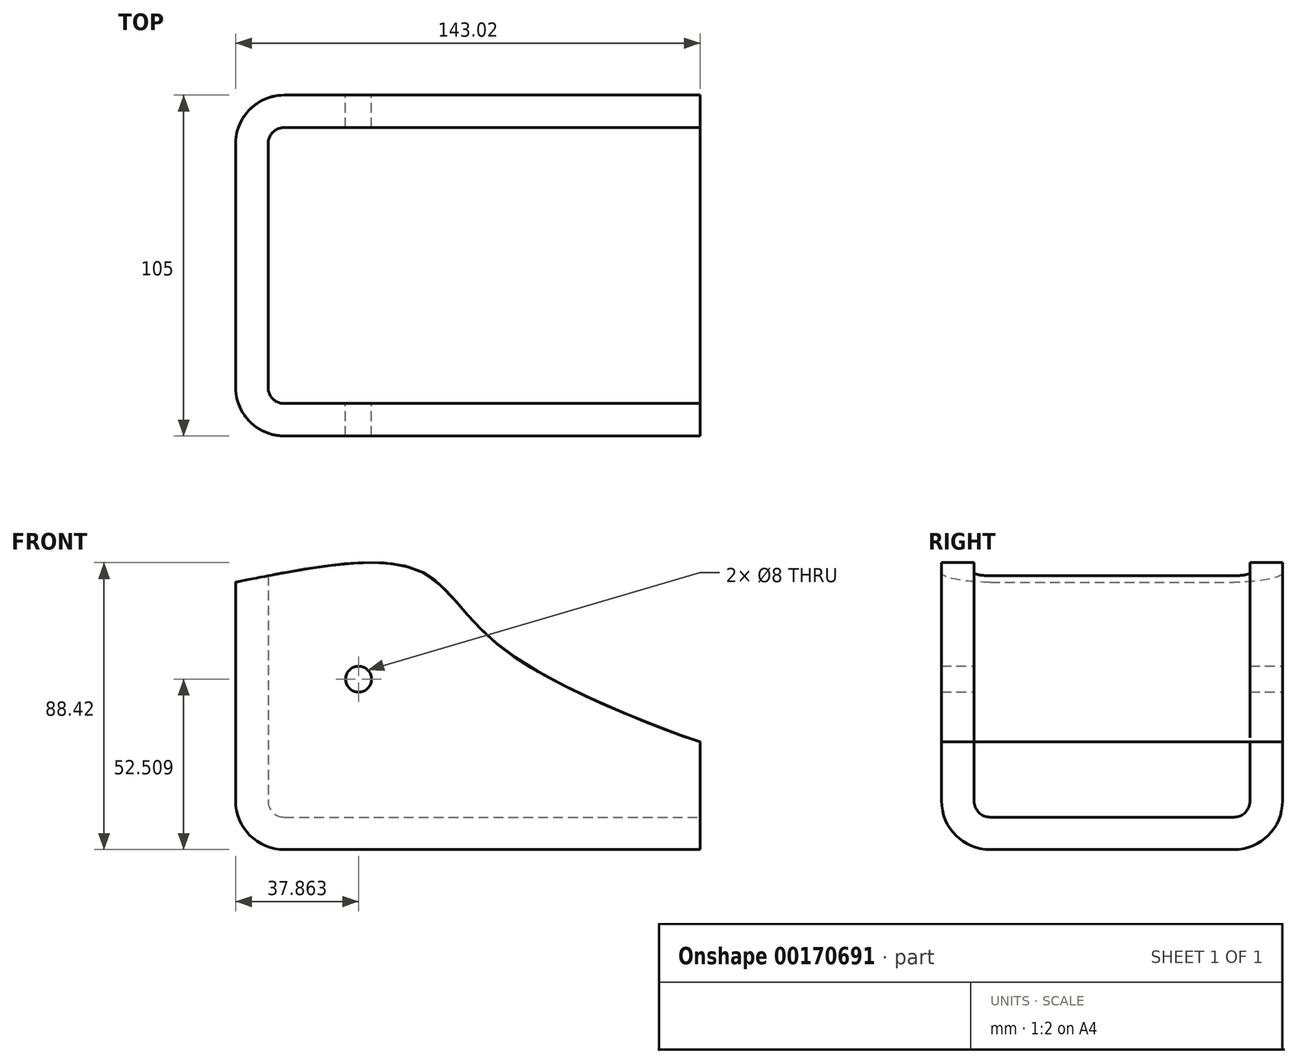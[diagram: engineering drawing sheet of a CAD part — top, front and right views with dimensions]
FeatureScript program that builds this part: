
annotation { "Feature Type Name" : "Feature", "Feature Type Description" : "" }
export const myFeature = defineFeature(function(context is Context, id is Id, definition is map)
    precondition{}
    {
        {
            var Q0;
            Q0=qCreatedBy(makeId("Front.planeOp"),FACE);
            var sketch = newSketch(context, id + "F0", { "sketchPlane" : qUnion([Q0])});
            skLineSegment(sketch, "E0.bottom", {"start": v(-80.05, 54.87) * mm, "end": v(101.14, 54.87) * mm});
            skLineSegment(sketch, "E0.top", {"start": v(-80.05, -66.57) * mm, "end": v(101.14, -66.57) * mm});
            skLineSegment(sketch, "E0.left", {"start": v(-80.05, 54.87) * mm, "end": v(-80.05, -66.57) * mm});
            skLineSegment(sketch, "E0.right", {"start": v(101.14, 54.87) * mm, "end": v(101.14, -66.57) * mm});
            skSolve(sketch);
        }
        {
            var Q0;
            Q0=makeQuery(id+"F0.imprint","IMPRINT",FACE,{"disambiguationData":[TD([[makeQuery(id+"F0.imprint","IMPRINT",EDGE,{"derivedFrom":sQuery(id+"F0.wireOp",EDGE,"E0.bottom")}),-1.0]])]});
            var sketch = newSketch(context, id + "F1", { "sketchPlane" : qUnion([Q0])});
            skSolve(sketch);
        }
        {
            var Q0;
            Q0=makeQuery(id+"F0.imprint","IMPRINT",FACE,{"disambiguationData":[TD([[makeQuery(id+"F0.imprint","IMPRINT",EDGE,{"derivedFrom":sQuery(id+"F0.wireOp",EDGE,"E0.bottom")}),-1.0]])]});
            var Q1;
            Q1=makeQuery(id+"F1.imprint","IMPRINT",FACE,{"disambiguationData":[TD([[makeQuery(id+"F1.imprint","IMPRINT",EDGE,{"derivedFrom":makeQuery(id+"F0.imprint","IMPRINT",EDGE,{"derivedFrom":sQuery(id+"F0.wireOp",EDGE,"E0.bottom")})}),-1.0]])]});
            extrude(context, id + "F2", {"entities" : qUnion([Q0, Q1]), "depth" : 82 * mm});
        }
        {
            var Q0;
            {var subQ0=sQuery(id+"F0.wireOp",EDGE,"E0.right");var subQ1=sQuery(id+"F0.wireOp",EDGE,"E0.left");var subQ2=sQuery(id+"F0.wireOp",EDGE,"E0.top");var subQ3=sQuery(id+"F0.wireOp",EDGE,"E0.bottom");Q0=makeQuery(id+"F2.opExtrude","CAP_FACE",FACE,{"disambiguationData":[OSD([subQ3,subQ2,subQ1,subQ0]),TDD([makeQuery(id+"F0.imprint","IMPRINT",EDGE,{"derivedFrom":subQ3}),makeQuery(id+"F0.imprint","IMPRINT",EDGE,{"derivedFrom":subQ2}),makeQuery(id+"F0.imprint","IMPRINT",EDGE,{"derivedFrom":subQ1}),makeQuery(id+"F0.imprint","IMPRINT",EDGE,{"derivedFrom":subQ0})])],"isStart":false});}
            var sketch = newSketch(context, id + "F3", { "sketchPlane" : qUnion([Q0])});
            skSolve(sketch);
        }
        {
            var Q0;
            {var subQ0=sQuery(id+"F0.wireOp",EDGE,"E0.bottom");Q0=makeQuery(id+"F3.imprint","IMPRINT",FACE,{"disambiguationData":[TD([[makeQuery(id+"F3.imprint","IMPRINT",EDGE,{"derivedFrom":makeQuery(id+"F2.opExtrude","CAP_EDGE",EDGE,{"disambiguationData":[OSD([subQ0]),TDD([makeQuery(id+"F0.imprint","IMPRINT",EDGE,{"derivedFrom":subQ0})])],"isStart":false})}),-1.0]])]});}
            var sketch = newSketch(context, id + "F4", { "sketchPlane" : qUnion([Q0])});
            skFitSpline(sketch, "E1", {"points": [v(-98.73, 12.92) * mm, v(-48.77, 13.61) * mm, v(25.93, 21.01) * mm, v(72.88, 0) * mm, v(123.53, -5.82) * mm, v(124.45, 27.72) * mm], "startDerivative": vector(232.7, -12.95) * mm, "endDerivative": vector(-57, 257.58) * mm});
            skLineSegment(sketch, "E2", {"start": v(-98.73, 12.92) * mm, "end": v(-98.73, 74.67) * mm});
            skLineSegment(sketch, "E3", {"start": v(-98.73, 74.67) * mm, "end": v(122.83, 74.67) * mm});
            skLineSegment(sketch, "E4", {"start": v(122.83, 74.67) * mm, "end": v(124.45, 27.72) * mm});
            skSolve(sketch);
        }
        {
            var Q0;
            {var subQ7=sQuery(id+"F0.wireOp",EDGE,"E0.bottom");var subQ8=makeQuery(id+"F3.imprint","IMPRINT",EDGE,{"derivedFrom":makeQuery(id+"F2.opExtrude","CAP_EDGE",EDGE,{"disambiguationData":[OSD([subQ7]),TDD([makeQuery(id+"F0.imprint","IMPRINT",EDGE,{"derivedFrom":subQ7})])],"isStart":false})});Q0=makeQuery(id+"F4.imprint","IMPRINT",FACE,{"disambiguationData":[TD([[makeQuery(id+"F4.imprint","IMPRINT",EDGE,{"derivedFrom":subQ8}),-1.0]])]});}
            extrude(context, id + "F5", {"entities" : qUnion([Q0]), "oppositeDirection" : true, "depth" : 209 * mm});
        }
        {
            var Q0;
            Q0=makeQuery(id+"F5.opExtrude","SWEPT_BODY",BODY,{"disambiguationData":[OSD([sQuery(id+"F0.wireOp",EDGE,"E0.bottom"),sQuery(id+"F0.wireOp",EDGE,"E0.left"),sQuery(id+"F0.wireOp",EDGE,"E0.right"),sQuery(id+"F4.wireOp",EDGE,"E1")])]});
            var Q1;
            {var subQ0=sQuery(id+"F0.wireOp",EDGE,"E0.right");var subQ1=sQuery(id+"F0.wireOp",EDGE,"E0.left");var subQ2=sQuery(id+"F0.wireOp",EDGE,"E0.top");var subQ3=sQuery(id+"F0.wireOp",EDGE,"E0.bottom");Q1=makeQuery(id+"F2.opExtrude","SWEPT_BODY",BODY,{"disambiguationData":[OSD([subQ3,subQ2,subQ1,subQ0]),TDD([makeQuery(id+"F0.imprint","IMPRINT",EDGE,{"derivedFrom":subQ3}),makeQuery(id+"F0.imprint","IMPRINT",EDGE,{"derivedFrom":subQ2}),makeQuery(id+"F0.imprint","IMPRINT",EDGE,{"derivedFrom":subQ1}),makeQuery(id+"F0.imprint","IMPRINT",EDGE,{"derivedFrom":subQ0})])]});}
            var Q2;
            {var subQ0=sQuery(id+"F0.wireOp",EDGE,"E0.right");var subQ1=sQuery(id+"F0.wireOp",EDGE,"E0.left");var subQ2=sQuery(id+"F0.wireOp",EDGE,"E0.top");var subQ3=sQuery(id+"F0.wireOp",EDGE,"E0.bottom");Q2=makeQuery(id+"F2.opExtrude","SWEPT_BODY",BODY,{"disambiguationData":[OSD([subQ3,subQ2,subQ1,subQ0]),TDD([makeQuery(id+"F1.imprint","IMPRINT",EDGE,{"derivedFrom":makeQuery(id+"F0.imprint","IMPRINT",EDGE,{"derivedFrom":subQ3})}),makeQuery(id+"F1.imprint","IMPRINT",EDGE,{"derivedFrom":makeQuery(id+"F0.imprint","IMPRINT",EDGE,{"derivedFrom":subQ2})}),makeQuery(id+"F1.imprint","IMPRINT",EDGE,{"derivedFrom":makeQuery(id+"F0.imprint","IMPRINT",EDGE,{"derivedFrom":subQ1})}),makeQuery(id+"F1.imprint","IMPRINT",EDGE,{"derivedFrom":makeQuery(id+"F0.imprint","IMPRINT",EDGE,{"derivedFrom":subQ0})})])]});}
            deleteBodies(context, id + "F6", {"entities" : qUnion([Q0, Q1, Q2])});
        }
        {
            var Q0;
            {var subQ0=sQuery(id+"F0.wireOp",EDGE,"E0.bottom");Q0=makeQuery(id+"F3.imprint","IMPRINT",FACE,{"disambiguationData":[TD([[makeQuery(id+"F3.imprint","IMPRINT",EDGE,{"derivedFrom":makeQuery(id+"F2.opExtrude","CAP_EDGE",EDGE,{"disambiguationData":[OSD([subQ0]),TDD([makeQuery(id+"F0.imprint","IMPRINT",EDGE,{"derivedFrom":subQ0})])],"isStart":false})}),-1.0]])]});}
            var sketch = newSketch(context, id + "F7", { "sketchPlane" : qUnion([Q0])});
            skLineSegment(sketch, "E5.top", {"start": v(-56.25, -55.4) * mm, "end": v(86.77, -55.4) * mm});
            skLineSegment(sketch, "E5.left", {"start": v(-56.25, 26.96) * mm, "end": v(-56.25, -55.4) * mm});
            skLineSegment(sketch, "E5.right", {"start": v(86.77, -22.15) * mm, "end": v(86.77, -55.4) * mm});
            skFitSpline(sketch, "E6", {"points": [v(-56.25, 26.96) * mm, v(0, 30.65) * mm, v(28.45, 4.75) * mm, v(86.77, -22.16) * mm, v(86.77, -22.15) * mm], "startDerivative": vector(192, 38.88) * mm, "endDerivative": vector(-1.24, 2.51) * mm});
            skSolve(sketch);
        }
        {
            var Q0;
            Q0 = qSketchRegion(id + "F7", true);
            extrude(context, id + "F8", {"entities" : qUnion([Q0]), "depth" : 105 * mm});
        }
        {
            var Q0;
            Q0=makeQuery(id+"F8.opExtrude","CAP_EDGE",EDGE,{"disambiguationData":[OSD([sQuery(id+"F7.wireOp",EDGE,"E5.top")])],"isStart":true});
            var Q1;
            Q1=makeQuery(id+"F8.opExtrude","SWEPT_EDGE",EDGE,{"disambiguationData":[OSD([sQuery(id+"F7.wireOp",EDGE,"E5.top"),sQuery(id+"F7.wireOp",EDGE,"E5.left")])]});
            var Q2;
            Q2=makeQuery(id+"F8.opExtrude","CAP_EDGE",EDGE,{"disambiguationData":[OSD([sQuery(id+"F7.wireOp",EDGE,"E5.left")])],"isStart":true});
            var Q3;
            Q3=makeQuery(id+"F8.opExtrude","CAP_EDGE",EDGE,{"disambiguationData":[OSD([sQuery(id+"F7.wireOp",EDGE,"E5.left")])],"isStart":false});
            var Q4;
            Q4=makeQuery(id+"F8.opExtrude","CAP_EDGE",EDGE,{"disambiguationData":[OSD([sQuery(id+"F7.wireOp",EDGE,"E5.top")])],"isStart":false});
            fillet(context, id + "F9", {"entities" : qUnion([Q0, Q1, Q2, Q3, Q4]), "radius" : 15 * mm, "tangentPropagation" : true, "allowEdgeOverflow" : false});
        }
        {
            var Q0;
            {var subQ0=sQuery(id+"F7.wireOp",EDGE,"E6");Q0=makeQuery(id+"F8.opExtrude","SWEPT_FACE",FACE,{"disambiguationData":[OSD([subQ0]),TDD([makeQuery(id+"F7.imprint","IMPRINT",EDGE,{"disambiguationData":[TD([[makeQuery(id+"F7.imprint","INTERSECT",VERTEX,{"derivedFrom":[sQuery(id+"F7.wireOp",EDGE,"E5.left"),subQ0]}),-1.0]])],"derivedFrom":subQ0})])]});}
            var Q1;
            {var subQ0=sQuery(id+"F7.wireOp",EDGE,"E5.right");Q1=makeQuery(id+"F8.opExtrude","SWEPT_FACE",FACE,{"disambiguationData":[OSD([subQ0]),TDD([makeQuery(id+"F7.imprint","IMPRINT",EDGE,{"disambiguationData":[TD([[makeQuery(id+"F7.imprint","INTERSECT",VERTEX,{"derivedFrom":[sQuery(id+"F7.wireOp",EDGE,"E5.top"),subQ0]}),1.0]])],"derivedFrom":subQ0})])]});}
            shell(context, id + "F10", {"entities" : qUnion([Q0, Q1]), "thickness" : 10 * mm});
        }
        {
            var Q0;
            Q0=qCreatedBy(makeId("Front.planeOp"),FACE);
            var sketch = newSketch(context, id + "F11", { "sketchPlane" : qUnion([Q0])});
            skCircle(sketch, "E7", {"center": v(-18.39, -2.9) * mm, "radius": 4 * mm});
            skSolve(sketch);
        }
        {
            var Q0;
            Q0 = qSketchRegion(id + "F11", true);
            extrude(context, id + "F12", {"entities" : qUnion([Q0]), "operationType" : NewBodyOperationType.REMOVE, "depth" : 268.2 * mm});
        }
    });
